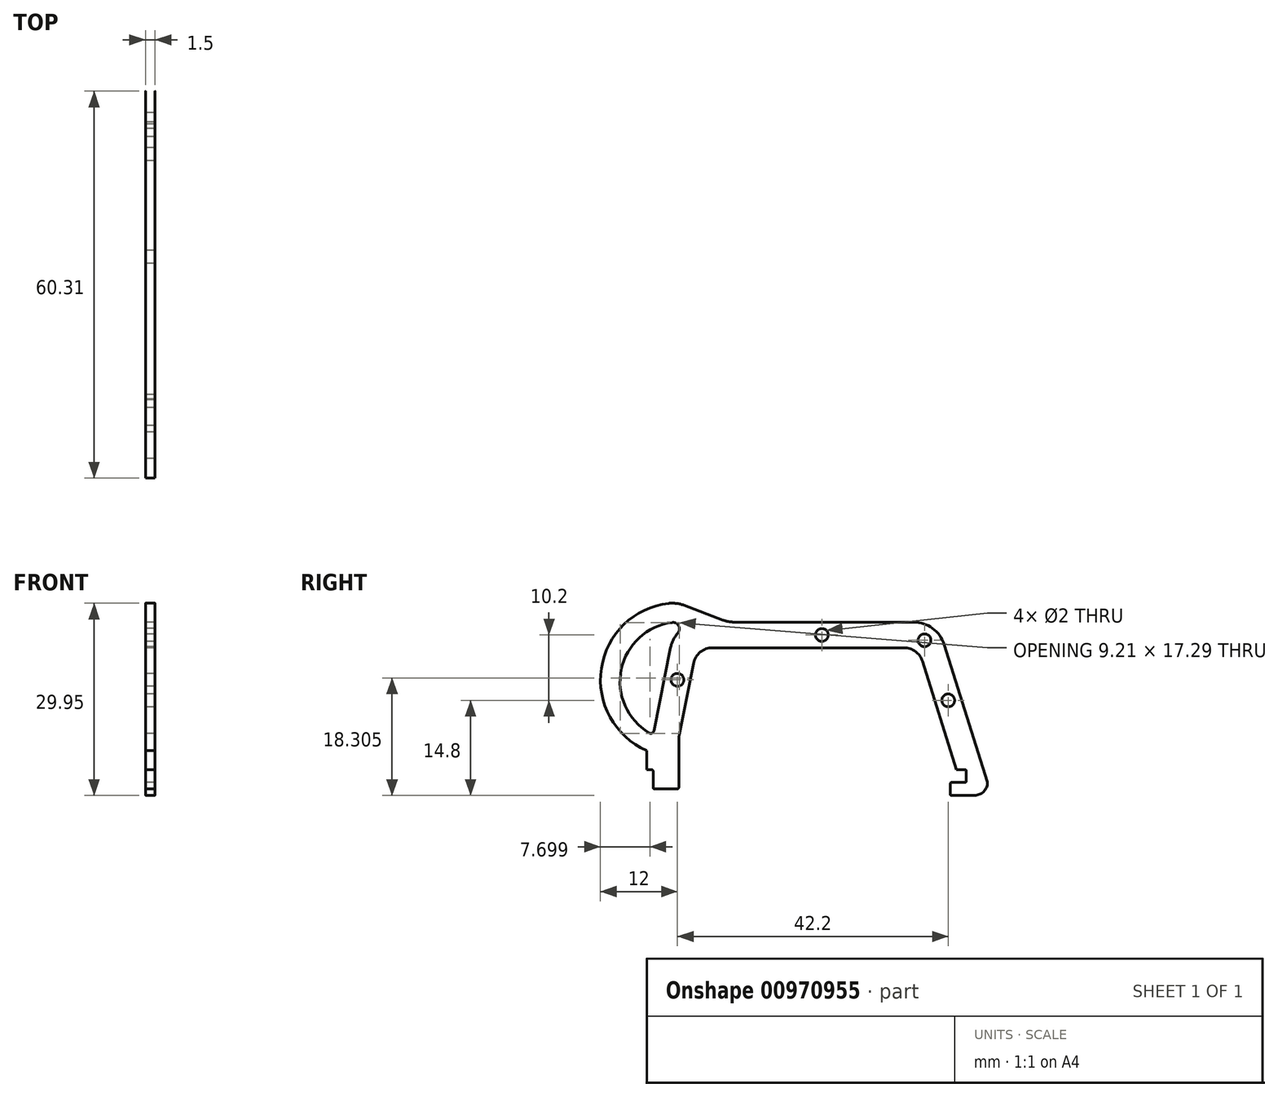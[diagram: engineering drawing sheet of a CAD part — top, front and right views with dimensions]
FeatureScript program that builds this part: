
annotation { "Feature Type Name" : "Feature", "Feature Type Description" : "" }
export const myFeature = defineFeature(function(context is Context, id is Id, definition is map)
    precondition{}
    {
        {
            var Q0;
            Q0=qCreatedBy(makeId("Right.planeOp"),FACE);
            var sketch = newSketch(context, id + "F0", { "sketchPlane" : qUnion([Q0])});
            skPoint(sketch, "E0.middle", {"position": v(0, 0) * mm});
            skLineSegment(sketch, "E1.0", {"start": v(-22.3, 6.5) * mm, "end": v(-22.3, -0.8) * mm});
            skLineSegment(sketch, "E2.0", {"start": v(-22.2, 7.49) * mm, "end": v(-19.98, 18.59) * mm});
            skPoint(sketch, "E3.visualSharp", {"position": v(-22.3, 7) * mm});
            skCircle(sketch, "E4", {"center": v(-22.5, 16) * mm, "radius": 1 * mm});
            skLineSegment(sketch, "E5", {"start": v(-26.3, -0.8) * mm, "end": v(-26.3, 1.8) * mm});
            skLineSegment(sketch, "E6", {"start": v(-26.5, 2) * mm, "end": v(-27.3, 2) * mm});
            skLineSegment(sketch, "E7.0", {"start": v(-26.17, 8.06) * mm, "end": v(-23.58, 20.98) * mm});
            skLineSegment(sketch, "E8.0", {"start": v(14.3, 25) * mm, "end": v(-13.65, 25) * mm});
            skLineSegment(sketch, "E9", {"start": v(21, 2) * mm, "end": v(15.68, 18.9) * mm});
            skLineSegment(sketch, "E10", {"start": v(-17.04, 21) * mm, "end": v(12.82, 21) * mm});
            skLineSegment(sketch, "E11.0", {"start": v(25.8, 0.07) * mm, "end": v(19.06, 21.5) * mm});
            skPoint(sketch, "E12.visualSharp", {"position": v(15.02, 21) * mm});
            skPoint(sketch, "E13.visualSharp", {"position": v(17.96, 25) * mm});
            skArc(sketch, "E14.filletArc", {"start": v(19.06, 21.5) * mm, "mid": v(17.25, 24.03) * mm, "end": v(14.3, 25) * mm});
            skArc(sketch, "E15.filletArc", {"start": v(15.68, 18.9) * mm, "mid": v(14.6, 20.42) * mm, "end": v(12.82, 21) * mm});
            skLineSegment(sketch, "E16.0", {"start": v(22.5, 0.2) * mm, "end": v(22.5, 1.8) * mm});
            skLineSegment(sketch, "E17.0", {"start": v(22.3, 2) * mm, "end": v(21, 2) * mm});
            skPoint(sketch, "E18.visualSharp", {"position": v(-22.78, 25) * mm});
            skArc(sketch, "E18.filletArc", {"start": v(-22.44, 23.3) * mm, "mid": v(-23.16, 22.21) * mm, "end": v(-23.58, 20.98) * mm});
            skPoint(sketch, "E19.visualSharp", {"position": v(-19.5, 21) * mm});
            skArc(sketch, "E19.filletArc", {"start": v(-17.04, 21) * mm, "mid": v(-18.94, 20.32) * mm, "end": v(-19.98, 18.59) * mm});
            skPoint(sketch, "E20.visualSharp", {"position": v(-26.3, 7.4) * mm});
            skArc(sketch, "E21.filletArc", {"start": v(-22.2, 7.49) * mm, "mid": v(-22.28, 7) * mm, "end": v(-22.3, 6.5) * mm});
            skPoint(sketch, "E22.visualSharp", {"position": v(25.81, 0.04) * mm});
            skLineSegment(sketch, "E23", {"start": v(-15.42, 25.32) * mm, "end": v(-21.53, 27.63) * mm});
            skArc(sketch, "E24", {"start": v(-23.86, 27.92) * mm, "mid": v(-34.37, 17.78) * mm, "end": v(-27.3, 5) * mm});
            skLineSegment(sketch, "E25", {"start": v(-22.5, 16) * mm, "end": v(-22.5, 28) * mm, "construction": true});
            skPoint(sketch, "E26.visualSharp", {"position": v(-14.56, 25) * mm});
            skArc(sketch, "E26.filletArc", {"start": v(-15.42, 25.32) * mm, "mid": v(-14.55, 25.08) * mm, "end": v(-13.65, 25) * mm});
            skArc(sketch, "E27", {"start": v(-23.32, 24.95) * mm, "mid": v(-31.26, 17.62) * mm, "end": v(-26.91, 7.73) * mm});
            skArc(sketch, "E28.filletArc", {"start": v(-26.91, 7.73) * mm, "mid": v(-26.45, 7.7) * mm, "end": v(-26.17, 8.06) * mm});
            skPoint(sketch, "E29.visualSharp", {"position": v(-20.1, 24.8) * mm});
            skArc(sketch, "E29.filletArc", {"start": v(-22.44, 23.3) * mm, "mid": v(-22.3, 24.42) * mm, "end": v(-23.32, 24.95) * mm});
            skPoint(sketch, "E30.visualSharp", {"position": v(-22.5, 28) * mm});
            skArc(sketch, "E30.filletArc", {"start": v(-21.53, 27.63) * mm, "mid": v(-22.68, 27.92) * mm, "end": v(-23.86, 27.92) * mm});
            skLineSegment(sketch, "E31", {"start": v(-12.47, 23) * mm, "end": v(13.56, 23) * mm, "construction": true});
            skLineSegment(sketch, "E32.0", {"start": v(22.9, 2.6) * mm, "end": v(17.37, 20.2) * mm, "construction": true});
            skCircle(sketch, "E33", {"center": v(0, 23) * mm, "radius": 1 * mm});
            skCircle(sketch, "E34", {"center": v(19.7, 12.8) * mm, "radius": 1 * mm});
            skLineSegment(sketch, "E35", {"start": v(0, 0.86) * mm, "end": v(0, 25) * mm, "construction": true});
            skCircle(sketch, "E36", {"center": v(16, 22.17) * mm, "radius": 1 * mm});
            skPoint(sketch, "E37.visualSharp", {"position": v(16.5, 23) * mm});
            skArc(sketch, "E37.filletArc", {"start": v(17.37, 20.2) * mm, "mid": v(15.92, 22.22) * mm, "end": v(13.56, 23) * mm, "construction": true});
            skLineSegment(sketch, "E38.top", {"start": v(23.81, -2) * mm, "end": v(20.2, -2) * mm});
            skLineSegment(sketch, "E38.left", {"start": v(25.81, 0) * mm, "end": v(25.81, 0) * mm});
            skPoint(sketch, "E39.visualSharp", {"position": v(22.5, 2) * mm});
            skArc(sketch, "E39.filletArc", {"start": v(22.5, 1.8) * mm, "mid": v(22.44, 1.94) * mm, "end": v(22.3, 2) * mm});
            skPoint(sketch, "E40.visualSharp", {"position": v(25.81, -2) * mm});
            skArc(sketch, "E40.filletArc", {"start": v(23.81, -2) * mm, "mid": v(25.22, -1.41) * mm, "end": v(25.81, 0) * mm});
            skLineSegment(sketch, "E41", {"start": v(20, -1.8) * mm, "end": v(20, -0.2) * mm});
            skLineSegment(sketch, "E42", {"start": v(22.3, 0) * mm, "end": v(20.2, 0) * mm});
            skPoint(sketch, "E43.visualSharp", {"position": v(22.5, 0) * mm});
            skArc(sketch, "E43.filletArc", {"start": v(22.3, 0) * mm, "mid": v(22.44, 0.06) * mm, "end": v(22.5, 0.2) * mm});
            skPoint(sketch, "E44.visualSharp", {"position": v(20, 0) * mm});
            skArc(sketch, "E44.filletArc", {"start": v(20.2, 0) * mm, "mid": v(20.06, -0.06) * mm, "end": v(20, -0.2) * mm});
            skPoint(sketch, "E45.visualSharp", {"position": v(20, -2) * mm});
            skArc(sketch, "E45.filletArc", {"start": v(20, -1.8) * mm, "mid": v(20.06, -1.94) * mm, "end": v(20.2, -2) * mm});
            skArc(sketch, "E46.filletArc", {"start": v(25.81, 0) * mm, "mid": v(25.8, 0.04) * mm, "end": v(25.8, 0.07) * mm});
            skLineSegment(sketch, "E47", {"start": v(-26.1, -1) * mm, "end": v(-22.5, -1) * mm});
            skPoint(sketch, "E48.visualSharp", {"position": v(-26.3, 2) * mm});
            skArc(sketch, "E48.filletArc", {"start": v(-26.3, 1.8) * mm, "mid": v(-26.36, 1.94) * mm, "end": v(-26.5, 2) * mm});
            skPoint(sketch, "E49.visualSharp", {"position": v(-26.3, -1) * mm});
            skArc(sketch, "E49.filletArc", {"start": v(-26.3, -0.8) * mm, "mid": v(-26.24, -0.94) * mm, "end": v(-26.1, -1) * mm});
            skPoint(sketch, "E50.visualSharp", {"position": v(-22.3, -1) * mm});
            skArc(sketch, "E50.filletArc", {"start": v(-22.5, -1) * mm, "mid": v(-22.36, -0.94) * mm, "end": v(-22.3, -0.8) * mm});
            skLineSegment(sketch, "E51", {"start": v(-27.3, 2) * mm, "end": v(-27.3, 5) * mm});
            skSolve(sketch);
        }
        {
            var Q0;
            Q0=makeQuery(id+"F0.imprint","IMPRINT",FACE,{"disambiguationData":[TD([[makeQuery(id+"F0.imprint","IMPRINT",EDGE,{"derivedFrom":sQuery(id+"F0.wireOp",EDGE,"E0.bottom")}),1.0]])]});
            var Q1;
            Q1=makeQuery(id+"F0.imprint","IMPRINT",FACE,{"disambiguationData":[TD([[makeQuery(id+"F0.imprint","IMPRINT",EDGE,{"derivedFrom":sQuery(id+"F0.wireOp",EDGE,"E1.0")}),-1.0]])]});
            extrude(context, id + "F1", {"entities" : qUnion([Q0, Q1]), "depth" : 1.5 * mm, "offsetDistance" : 25 * mm, "symmetric" : true});
        }
    });
